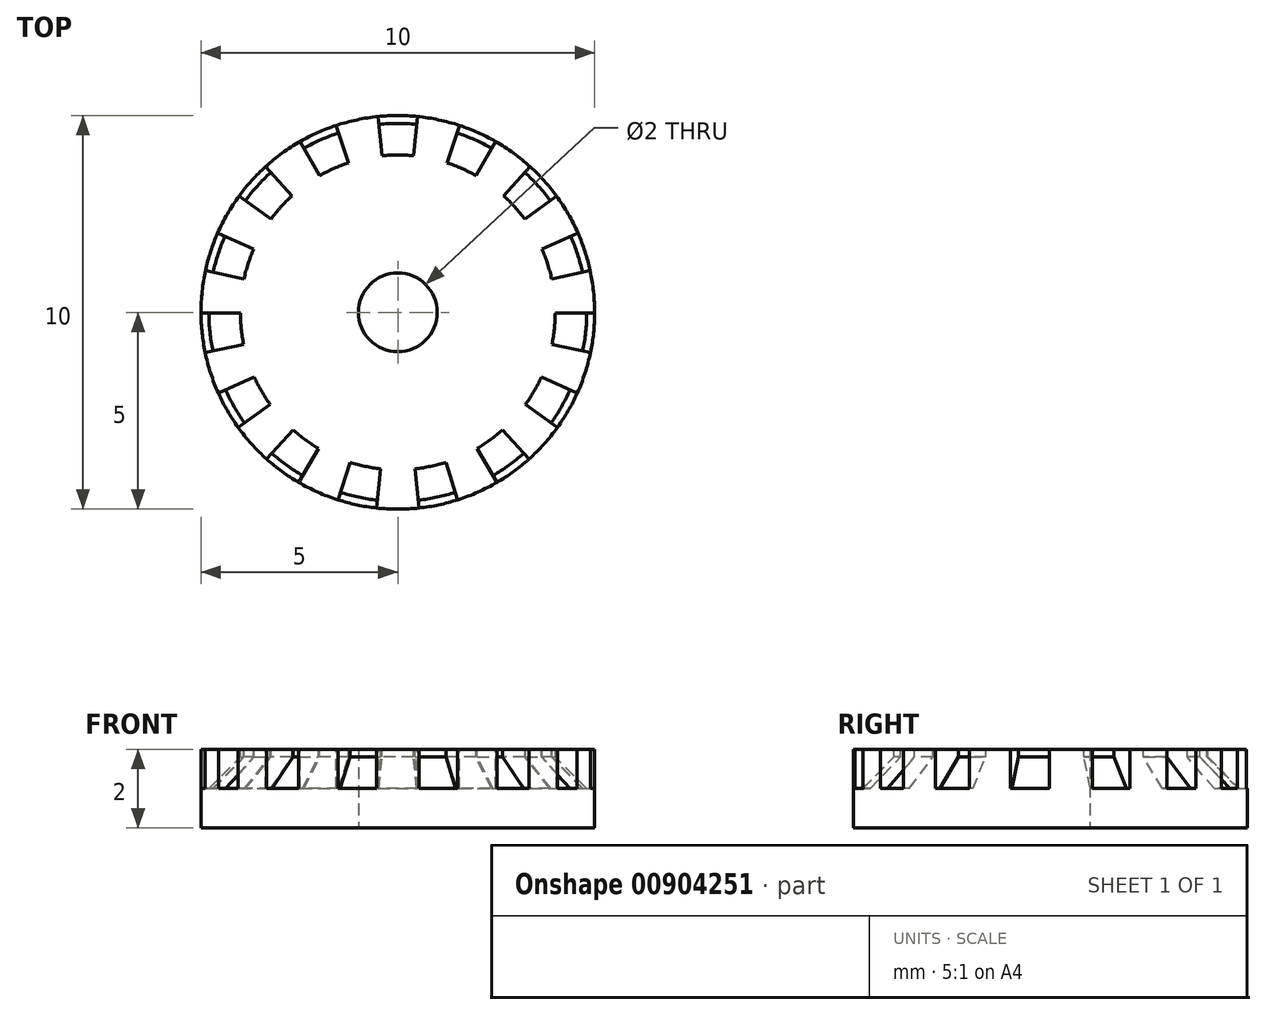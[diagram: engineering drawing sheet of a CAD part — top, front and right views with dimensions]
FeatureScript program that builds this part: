
annotation { "Feature Type Name" : "Feature", "Feature Type Description" : "" }
export const myFeature = defineFeature(function(context is Context, id is Id, definition is map)
    precondition{}
    {
        {
            var Q0;
            Q0=qCreatedBy(makeId("Front.planeOp"),FACE);
            var sketch = newSketch(context, id + "F0", { "sketchPlane" : qUnion([Q0])});
            skLineSegment(sketch, "E0.bottom", {"start": v(0, 0) * mm, "end": v(-5, 0) * mm});
            skLineSegment(sketch, "E0.top", {"start": v(0, 2) * mm, "end": v(-5, 2) * mm});
            skLineSegment(sketch, "E0.left", {"start": v(0, 0) * mm, "end": v(0, 2) * mm});
            skLineSegment(sketch, "E0.right", {"start": v(-5, 0) * mm, "end": v(-5, 2) * mm});
            skLineSegment(sketch, "E1", {"start": v(-1, 2) * mm, "end": v(-1, 0) * mm});
            skSolve(sketch);
        }
        {
            var Q0;
            {var subQ0=sQuery(id+"F0.wireOp",EDGE,"E0.right");Q0=makeQuery(id+"F0.imprint","IMPRINT",FACE,{"disambiguationData":[TD([[makeQuery(id+"F0.imprint","IMPRINT",EDGE,{"derivedFrom":subQ0}),-1.0]])]});}
            var Q1;
            Q1=sQuery(id+"F0.wireOp",EDGE,"E0.left");
            revolve(context, id + "F1", {"surfaceOperationType" : NewSurfaceOperationType.NEW, "entities" : qUnion([Q0]), "axis" : qUnion([Q1]), "revolveType" : RevolveType.FULL});
        }
        {
            var Q0;
            Q0=makeQuery(id+"F1.opRevolve","SWEPT_FACE",FACE,{"disambiguationData":[OSD([sQuery(id+"F0.wireOp",EDGE,"E0.top")])]});
            var sketch = newSketch(context, id + "F2", { "sketchPlane" : qUnion([Q0])});
            skLineSegment(sketch, "E2", {"start": v(0, 0) * mm, "end": v(0, 5) * mm});
            skLineSegment(sketch, "E3", {"start": v(-0.5, 4.97) * mm, "end": v(0.5, 4.97) * mm});
            skLineSegment(sketch, "E4", {"start": v(0, 0) * mm, "end": v(-0.5, 4.97) * mm});
            skLineSegment(sketch, "E5", {"start": v(0, 0) * mm, "end": v(0.5, 4.97) * mm});
            skCircle(sketch, "E6", {"center": v(0, 0) * mm, "radius": 4 * mm});
            skLineSegment(sketch, "E7", {"start": v(0, 0) * mm, "end": v(4, 0) * mm});
            skLineSegment(sketch, "E8", {"start": v(4, 0) * mm, "end": v(5, 0) * mm});
            skLineSegment(sketch, "E9.1.0", {"start": v(0, 0) * mm, "end": v(-2.48, 4.34) * mm});
            skLineSegment(sketch, "E9.1.1", {"start": v(0, 0) * mm, "end": v(-1.57, 4.75) * mm});
            skLineSegment(sketch, "E9.2.0", {"start": v(0, 0) * mm, "end": v(-4.03, 2.96) * mm});
            skLineSegment(sketch, "E9.2.1", {"start": v(0, 0) * mm, "end": v(-3.36, 3.7) * mm});
            skLineSegment(sketch, "E10.2.3.0", {"start": v(0, 0) * mm, "end": v(-4.89, 1.06) * mm});
            skLineSegment(sketch, "E10.3.3.0", {"start": v(0, 0) * mm, "end": v(-4.58, 2.01) * mm});
            skLineSegment(sketch, "E10.2.4.0", {"start": v(0, 0) * mm, "end": v(-4.9, -1.02) * mm});
            skLineSegment(sketch, "E10.3.4.0", {"start": v(0, 0) * mm, "end": v(-5, -0.02) * mm});
            skLineSegment(sketch, "E10.2.5.0", {"start": v(0, 0) * mm, "end": v(-4.06, -2.92) * mm});
            skLineSegment(sketch, "E10.3.5.0", {"start": v(0, 0) * mm, "end": v(-4.56, -2.05) * mm});
            skLineSegment(sketch, "E10.2.6.0", {"start": v(0, 0) * mm, "end": v(-2.52, -4.32) * mm});
            skLineSegment(sketch, "E10.3.6.0", {"start": v(0, 0) * mm, "end": v(-3.33, -3.73) * mm});
            skLineSegment(sketch, "E10.2.7.0", {"start": v(0, 0) * mm, "end": v(-0.55, -4.97) * mm});
            skLineSegment(sketch, "E10.3.7.0", {"start": v(0, 0) * mm, "end": v(-1.52, -4.76) * mm});
            skLineSegment(sketch, "E10.2.8.0", {"start": v(0, 0) * mm, "end": v(1.52, -4.76) * mm});
            skLineSegment(sketch, "E10.3.8.0", {"start": v(0, 0) * mm, "end": v(0.55, -4.97) * mm});
            skLineSegment(sketch, "E10.2.9.0", {"start": v(0, 0) * mm, "end": v(3.33, -3.73) * mm});
            skLineSegment(sketch, "E10.3.9.0", {"start": v(0, 0) * mm, "end": v(2.52, -4.32) * mm});
            skLineSegment(sketch, "E10.2.10.0", {"start": v(0, 0) * mm, "end": v(4.56, -2.05) * mm});
            skLineSegment(sketch, "E10.3.10.0", {"start": v(0, 0) * mm, "end": v(4.06, -2.92) * mm});
            skLineSegment(sketch, "E10.2.11.0", {"start": v(0, 0) * mm, "end": v(5, -0.02) * mm});
            skLineSegment(sketch, "E10.3.11.0", {"start": v(0, 0) * mm, "end": v(4.9, -1.02) * mm});
            skLineSegment(sketch, "E10.2.12.0", {"start": v(0, 0) * mm, "end": v(4.58, 2.01) * mm});
            skLineSegment(sketch, "E10.3.12.0", {"start": v(0, 0) * mm, "end": v(4.89, 1.06) * mm});
            skLineSegment(sketch, "E10.2.13.0", {"start": v(0, 0) * mm, "end": v(3.36, 3.7) * mm});
            skLineSegment(sketch, "E10.3.13.0", {"start": v(0, 0) * mm, "end": v(4.03, 2.96) * mm});
            skLineSegment(sketch, "E10.2.14.0", {"start": v(0, 0) * mm, "end": v(1.57, 4.75) * mm});
            skLineSegment(sketch, "E10.3.14.0", {"start": v(0, 0) * mm, "end": v(2.48, 4.34) * mm});
            skSolve(sketch);
        }
        {
            var Q0;
            {var subQ0=sQuery(id+"F2.wireOp",EDGE,"E6");var subQ1=sQuery(id+"F2.wireOp",EDGE,"E2");var subQ2=makeQuery(id+"F2.imprint","INTERSECT",VERTEX,{"derivedFrom":[subQ1,subQ0]});Q0=makeQuery(id+"F2.imprint","IMPRINT",FACE,{"disambiguationData":[TD([[makeQuery(id+"F2.imprint","IMPRINT",EDGE,{"disambiguationData":[TD([[subQ2,-1.0]])],"derivedFrom":subQ1}),1.0]])]});}
            var Q1;
            {var subQ0=sQuery(id+"F2.wireOp",EDGE,"E6");var subQ1=sQuery(id+"F2.wireOp",EDGE,"E2");var subQ2=makeQuery(id+"F2.imprint","INTERSECT",VERTEX,{"derivedFrom":[subQ1,subQ0]});Q1=makeQuery(id+"F2.imprint","IMPRINT",FACE,{"disambiguationData":[TD([[makeQuery(id+"F2.imprint","IMPRINT",EDGE,{"disambiguationData":[TD([[subQ2,-1.0]])],"derivedFrom":subQ1}),-1.0]])]});}
            var Q2;
            {var subQ0=sQuery(id+"F2.wireOp",EDGE,"E2");var subQ3=sQuery(id+"F2.wireOp",EDGE,"E3");var subQ4=makeQuery(id+"F2.imprint","INTERSECT",VERTEX,{"derivedFrom":[subQ0,subQ3]});Q2=makeQuery(id+"F2.imprint","IMPRINT",FACE,{"disambiguationData":[TD([[makeQuery(id+"F2.imprint","IMPRINT",EDGE,{"disambiguationData":[TD([[subQ4,-1.0]])],"derivedFrom":subQ0}),-1.0]])]});}
            var Q3;
            {var subQ0=sQuery(id+"F2.wireOp",EDGE,"E2");var subQ3=sQuery(id+"F2.wireOp",EDGE,"E3");var subQ4=makeQuery(id+"F2.imprint","INTERSECT",VERTEX,{"derivedFrom":[subQ0,subQ3]});Q3=makeQuery(id+"F2.imprint","IMPRINT",FACE,{"disambiguationData":[TD([[makeQuery(id+"F2.imprint","IMPRINT",EDGE,{"disambiguationData":[TD([[subQ4,-1.0]])],"derivedFrom":subQ0}),1.0]])]});}
            var Q4;
            {var subQ0=sQuery(id+"F2.wireOp",EDGE,"E10.3.14.0");var subQ1=sQuery(id+"F2.wireOp",EDGE,"E6");var subQ2=makeQuery(id+"F2.imprint","INTERSECT",VERTEX,{"derivedFrom":[subQ1,subQ0]});Q4=makeQuery(id+"F2.imprint","IMPRINT",FACE,{"disambiguationData":[TD([[makeQuery(id+"F2.imprint","IMPRINT",EDGE,{"disambiguationData":[TD([[subQ2,-1.0]])],"derivedFrom":subQ1}),-1.0]])]});}
            var Q5;
            {var subQ0=sQuery(id+"F2.wireOp",EDGE,"E10.3.13.0");var subQ1=sQuery(id+"F2.wireOp",EDGE,"E6");var subQ2=makeQuery(id+"F2.imprint","INTERSECT",VERTEX,{"derivedFrom":[subQ1,subQ0]});Q5=makeQuery(id+"F2.imprint","IMPRINT",FACE,{"disambiguationData":[TD([[makeQuery(id+"F2.imprint","IMPRINT",EDGE,{"disambiguationData":[TD([[subQ2,-1.0]])],"derivedFrom":subQ1}),-1.0]])]});}
            var Q6;
            {var subQ0=sQuery(id+"F2.wireOp",EDGE,"E10.3.12.0");var subQ1=sQuery(id+"F2.wireOp",EDGE,"E6");var subQ2=makeQuery(id+"F2.imprint","INTERSECT",VERTEX,{"derivedFrom":[subQ1,subQ0]});Q6=makeQuery(id+"F2.imprint","IMPRINT",FACE,{"disambiguationData":[TD([[makeQuery(id+"F2.imprint","IMPRINT",EDGE,{"disambiguationData":[TD([[subQ2,-1.0]])],"derivedFrom":subQ1}),-1.0]])]});}
            var Q7;
            {var subQ0=sQuery(id+"F2.wireOp",EDGE,"E10.3.11.0");var subQ1=sQuery(id+"F2.wireOp",EDGE,"E6");var subQ2=makeQuery(id+"F2.imprint","INTERSECT",VERTEX,{"derivedFrom":[subQ1,subQ0]});Q7=makeQuery(id+"F2.imprint","IMPRINT",FACE,{"disambiguationData":[TD([[makeQuery(id+"F2.imprint","IMPRINT",EDGE,{"disambiguationData":[TD([[subQ2,-1.0]])],"derivedFrom":subQ1}),-1.0]])]});}
            var Q8;
            {var subQ0=sQuery(id+"F2.wireOp",EDGE,"E10.3.10.0");var subQ1=sQuery(id+"F2.wireOp",EDGE,"E6");var subQ2=makeQuery(id+"F2.imprint","INTERSECT",VERTEX,{"derivedFrom":[subQ1,subQ0]});Q8=makeQuery(id+"F2.imprint","IMPRINT",FACE,{"disambiguationData":[TD([[makeQuery(id+"F2.imprint","IMPRINT",EDGE,{"disambiguationData":[TD([[subQ2,-1.0]])],"derivedFrom":subQ1}),-1.0]])]});}
            var Q9;
            {var subQ0=sQuery(id+"F2.wireOp",EDGE,"E10.3.9.0");var subQ1=sQuery(id+"F2.wireOp",EDGE,"E6");var subQ2=makeQuery(id+"F2.imprint","INTERSECT",VERTEX,{"derivedFrom":[subQ1,subQ0]});Q9=makeQuery(id+"F2.imprint","IMPRINT",FACE,{"disambiguationData":[TD([[makeQuery(id+"F2.imprint","IMPRINT",EDGE,{"disambiguationData":[TD([[subQ2,-1.0]])],"derivedFrom":subQ1}),-1.0]])]});}
            var Q10;
            {var subQ0=sQuery(id+"F2.wireOp",EDGE,"E10.3.8.0");var subQ1=sQuery(id+"F2.wireOp",EDGE,"E6");var subQ2=makeQuery(id+"F2.imprint","INTERSECT",VERTEX,{"derivedFrom":[subQ1,subQ0]});Q10=makeQuery(id+"F2.imprint","IMPRINT",FACE,{"disambiguationData":[TD([[makeQuery(id+"F2.imprint","IMPRINT",EDGE,{"disambiguationData":[TD([[subQ2,-1.0]])],"derivedFrom":subQ1}),-1.0]])]});}
            var Q11;
            {var subQ0=sQuery(id+"F2.wireOp",EDGE,"E10.3.7.0");var subQ1=sQuery(id+"F2.wireOp",EDGE,"E6");var subQ2=makeQuery(id+"F2.imprint","INTERSECT",VERTEX,{"derivedFrom":[subQ1,subQ0]});Q11=makeQuery(id+"F2.imprint","IMPRINT",FACE,{"disambiguationData":[TD([[makeQuery(id+"F2.imprint","IMPRINT",EDGE,{"disambiguationData":[TD([[subQ2,-1.0]])],"derivedFrom":subQ1}),-1.0]])]});}
            var Q12;
            {var subQ0=sQuery(id+"F2.wireOp",EDGE,"E10.3.6.0");var subQ1=sQuery(id+"F2.wireOp",EDGE,"E6");var subQ2=makeQuery(id+"F2.imprint","INTERSECT",VERTEX,{"derivedFrom":[subQ1,subQ0]});Q12=makeQuery(id+"F2.imprint","IMPRINT",FACE,{"disambiguationData":[TD([[makeQuery(id+"F2.imprint","IMPRINT",EDGE,{"disambiguationData":[TD([[subQ2,-1.0]])],"derivedFrom":subQ1}),-1.0]])]});}
            var Q13;
            {var subQ0=sQuery(id+"F2.wireOp",EDGE,"E10.3.5.0");var subQ1=sQuery(id+"F2.wireOp",EDGE,"E6");var subQ2=makeQuery(id+"F2.imprint","INTERSECT",VERTEX,{"derivedFrom":[subQ1,subQ0]});Q13=makeQuery(id+"F2.imprint","IMPRINT",FACE,{"disambiguationData":[TD([[makeQuery(id+"F2.imprint","IMPRINT",EDGE,{"disambiguationData":[TD([[subQ2,-1.0]])],"derivedFrom":subQ1}),-1.0]])]});}
            var Q14;
            {var subQ0=sQuery(id+"F2.wireOp",EDGE,"E10.3.4.0");var subQ1=sQuery(id+"F2.wireOp",EDGE,"E6");var subQ2=makeQuery(id+"F2.imprint","INTERSECT",VERTEX,{"derivedFrom":[subQ1,subQ0]});Q14=makeQuery(id+"F2.imprint","IMPRINT",FACE,{"disambiguationData":[TD([[makeQuery(id+"F2.imprint","IMPRINT",EDGE,{"disambiguationData":[TD([[subQ2,-1.0]])],"derivedFrom":subQ1}),-1.0]])]});}
            var Q15;
            {var subQ0=sQuery(id+"F2.wireOp",EDGE,"E10.3.3.0");var subQ1=sQuery(id+"F2.wireOp",EDGE,"E6");var subQ2=makeQuery(id+"F2.imprint","INTERSECT",VERTEX,{"derivedFrom":[subQ1,subQ0]});Q15=makeQuery(id+"F2.imprint","IMPRINT",FACE,{"disambiguationData":[TD([[makeQuery(id+"F2.imprint","IMPRINT",EDGE,{"disambiguationData":[TD([[subQ2,-1.0]])],"derivedFrom":subQ1}),-1.0]])]});}
            var Q16;
            {var subQ0=sQuery(id+"F2.wireOp",EDGE,"E9.2.1");var subQ1=sQuery(id+"F2.wireOp",EDGE,"E6");var subQ2=makeQuery(id+"F2.imprint","INTERSECT",VERTEX,{"derivedFrom":[subQ1,subQ0]});Q16=makeQuery(id+"F2.imprint","IMPRINT",FACE,{"disambiguationData":[TD([[makeQuery(id+"F2.imprint","IMPRINT",EDGE,{"disambiguationData":[TD([[subQ2,-1.0]])],"derivedFrom":subQ1}),-1.0]])]});}
            var Q17;
            {var subQ0=sQuery(id+"F2.wireOp",EDGE,"E9.1.1");var subQ1=sQuery(id+"F2.wireOp",EDGE,"E6");var subQ2=makeQuery(id+"F2.imprint","INTERSECT",VERTEX,{"derivedFrom":[subQ1,subQ0]});Q17=makeQuery(id+"F2.imprint","IMPRINT",FACE,{"disambiguationData":[TD([[makeQuery(id+"F2.imprint","IMPRINT",EDGE,{"disambiguationData":[TD([[subQ2,-1.0]])],"derivedFrom":subQ1}),-1.0]])]});}
            extrude(context, id + "F3", {"entities" : qUnion([Q0, Q1, Q2, Q3, Q4, Q5, Q6, Q7, Q8, Q9, Q10, Q11, Q12, Q13, Q14, Q15, Q16, Q17]), "operationType" : NewBodyOperationType.REMOVE, "oppositeDirection" : true, "depth" : 1 * mm, "offsetDistance" : 25 * mm});
        }
        {
            var Q0;
            {var subQ0=sQuery(id+"F2.wireOp",EDGE,"E6");Q0=makeQuery(id+"F3.boolean.opBoolean","COPY",EDGE,{"derivedFrom":makeQuery(id+"F3.opExtrude","CAP_EDGE",EDGE,{"disambiguationData":[OSD([subQ0]),TDD([makeQuery(id+"F2.imprint","IMPRINT",EDGE,{"disambiguationData":[TD([[makeQuery(id+"F2.imprint","INTERSECT",VERTEX,{"derivedFrom":[subQ0,sQuery(id+"F2.wireOp",EDGE,"E10.3.4.0")]}),-1.0]])],"derivedFrom":subQ0})])],"isStart":false})});}
            var Q1;
            {var subQ0=sQuery(id+"F2.wireOp",EDGE,"E6");Q1=makeQuery(id+"F3.boolean.opBoolean","COPY",EDGE,{"derivedFrom":makeQuery(id+"F3.opExtrude","CAP_EDGE",EDGE,{"disambiguationData":[OSD([subQ0]),TDD([makeQuery(id+"F2.imprint","IMPRINT",EDGE,{"disambiguationData":[TD([[makeQuery(id+"F2.imprint","INTERSECT",VERTEX,{"derivedFrom":[subQ0,sQuery(id+"F2.wireOp",EDGE,"E10.3.5.0")]}),-1.0]])],"derivedFrom":subQ0})])],"isStart":false})});}
            var Q2;
            {var subQ0=sQuery(id+"F2.wireOp",EDGE,"E6");Q2=makeQuery(id+"F3.boolean.opBoolean","COPY",EDGE,{"derivedFrom":makeQuery(id+"F3.opExtrude","CAP_EDGE",EDGE,{"disambiguationData":[OSD([subQ0]),TDD([makeQuery(id+"F2.imprint","IMPRINT",EDGE,{"disambiguationData":[TD([[makeQuery(id+"F2.imprint","INTERSECT",VERTEX,{"derivedFrom":[subQ0,sQuery(id+"F2.wireOp",EDGE,"E10.3.6.0")]}),-1.0]])],"derivedFrom":subQ0})])],"isStart":false})});}
            var Q3;
            {var subQ0=sQuery(id+"F2.wireOp",EDGE,"E6");Q3=makeQuery(id+"F3.boolean.opBoolean","COPY",EDGE,{"derivedFrom":makeQuery(id+"F3.opExtrude","CAP_EDGE",EDGE,{"disambiguationData":[OSD([subQ0]),TDD([makeQuery(id+"F2.imprint","IMPRINT",EDGE,{"disambiguationData":[TD([[makeQuery(id+"F2.imprint","INTERSECT",VERTEX,{"derivedFrom":[subQ0,sQuery(id+"F2.wireOp",EDGE,"E10.3.7.0")]}),-1.0]])],"derivedFrom":subQ0})])],"isStart":false})});}
            var Q4;
            {var subQ0=sQuery(id+"F2.wireOp",EDGE,"E6");Q4=makeQuery(id+"F3.boolean.opBoolean","COPY",EDGE,{"derivedFrom":makeQuery(id+"F3.opExtrude","CAP_EDGE",EDGE,{"disambiguationData":[OSD([subQ0]),TDD([makeQuery(id+"F2.imprint","IMPRINT",EDGE,{"disambiguationData":[TD([[makeQuery(id+"F2.imprint","INTERSECT",VERTEX,{"derivedFrom":[subQ0,sQuery(id+"F2.wireOp",EDGE,"E10.3.8.0")]}),-1.0]])],"derivedFrom":subQ0})])],"isStart":false})});}
            var Q5;
            {var subQ0=sQuery(id+"F2.wireOp",EDGE,"E6");Q5=makeQuery(id+"F3.boolean.opBoolean","COPY",EDGE,{"derivedFrom":makeQuery(id+"F3.opExtrude","CAP_EDGE",EDGE,{"disambiguationData":[OSD([subQ0]),TDD([makeQuery(id+"F2.imprint","IMPRINT",EDGE,{"disambiguationData":[TD([[makeQuery(id+"F2.imprint","INTERSECT",VERTEX,{"derivedFrom":[subQ0,sQuery(id+"F2.wireOp",EDGE,"E10.3.9.0")]}),-1.0]])],"derivedFrom":subQ0})])],"isStart":false})});}
            var Q6;
            {var subQ0=sQuery(id+"F2.wireOp",EDGE,"E6");Q6=makeQuery(id+"F3.boolean.opBoolean","COPY",EDGE,{"derivedFrom":makeQuery(id+"F3.opExtrude","CAP_EDGE",EDGE,{"disambiguationData":[OSD([subQ0]),TDD([makeQuery(id+"F2.imprint","IMPRINT",EDGE,{"disambiguationData":[TD([[makeQuery(id+"F2.imprint","INTERSECT",VERTEX,{"derivedFrom":[subQ0,sQuery(id+"F2.wireOp",EDGE,"E10.3.10.0")]}),-1.0]])],"derivedFrom":subQ0})])],"isStart":false})});}
            var Q7;
            {var subQ0=sQuery(id+"F2.wireOp",EDGE,"E6");Q7=makeQuery(id+"F3.boolean.opBoolean","COPY",EDGE,{"derivedFrom":makeQuery(id+"F3.opExtrude","CAP_EDGE",EDGE,{"disambiguationData":[OSD([subQ0]),TDD([makeQuery(id+"F2.imprint","IMPRINT",EDGE,{"disambiguationData":[TD([[makeQuery(id+"F2.imprint","INTERSECT",VERTEX,{"derivedFrom":[subQ0,sQuery(id+"F2.wireOp",EDGE,"E10.3.11.0")]}),-1.0]])],"derivedFrom":subQ0})])],"isStart":false})});}
            var Q8;
            {var subQ0=sQuery(id+"F2.wireOp",EDGE,"E6");Q8=makeQuery(id+"F3.boolean.opBoolean","COPY",EDGE,{"derivedFrom":makeQuery(id+"F3.opExtrude","CAP_EDGE",EDGE,{"disambiguationData":[OSD([subQ0]),TDD([makeQuery(id+"F2.imprint","IMPRINT",EDGE,{"disambiguationData":[TD([[makeQuery(id+"F2.imprint","INTERSECT",VERTEX,{"derivedFrom":[subQ0,sQuery(id+"F2.wireOp",EDGE,"E10.3.12.0")]}),-1.0]])],"derivedFrom":subQ0})])],"isStart":false})});}
            var Q9;
            {var subQ0=sQuery(id+"F2.wireOp",EDGE,"E6");Q9=makeQuery(id+"F3.boolean.opBoolean","COPY",EDGE,{"derivedFrom":makeQuery(id+"F3.opExtrude","CAP_EDGE",EDGE,{"disambiguationData":[OSD([subQ0]),TDD([makeQuery(id+"F2.imprint","IMPRINT",EDGE,{"disambiguationData":[TD([[makeQuery(id+"F2.imprint","INTERSECT",VERTEX,{"derivedFrom":[subQ0,sQuery(id+"F2.wireOp",EDGE,"E10.3.13.0")]}),-1.0]])],"derivedFrom":subQ0})])],"isStart":false})});}
            var Q10;
            {var subQ0=sQuery(id+"F2.wireOp",EDGE,"E6");Q10=makeQuery(id+"F3.boolean.opBoolean","COPY",EDGE,{"derivedFrom":makeQuery(id+"F3.opExtrude","CAP_EDGE",EDGE,{"disambiguationData":[OSD([subQ0]),TDD([makeQuery(id+"F2.imprint","IMPRINT",EDGE,{"disambiguationData":[TD([[makeQuery(id+"F2.imprint","INTERSECT",VERTEX,{"derivedFrom":[subQ0,sQuery(id+"F2.wireOp",EDGE,"E10.3.14.0")]}),-1.0]])],"derivedFrom":subQ0})])],"isStart":false})});}
            var Q11;
            {var subQ0=sQuery(id+"F2.wireOp",EDGE,"E6");var subQ1=makeQuery(id+"F2.imprint","INTERSECT",VERTEX,{"derivedFrom":[sQuery(id+"F2.wireOp",EDGE,"E2"),subQ0]});Q11=makeQuery(id+"F3.boolean.opBoolean","COPY",EDGE,{"derivedFrom":makeQuery(id+"F3.opExtrude","CAP_EDGE",EDGE,{"disambiguationData":[OSD([subQ0]),TDD([makeQuery(id+"F2.imprint","IMPRINT",EDGE,{"disambiguationData":[TD([[subQ1,1.0]])],"derivedFrom":subQ0}),makeQuery(id+"F2.imprint","IMPRINT",EDGE,{"disambiguationData":[TD([[subQ1,-1.0]])],"derivedFrom":subQ0})])],"isStart":false})});}
            var Q12;
            {var subQ0=sQuery(id+"F2.wireOp",EDGE,"E6");Q12=makeQuery(id+"F3.boolean.opBoolean","COPY",EDGE,{"derivedFrom":makeQuery(id+"F3.opExtrude","CAP_EDGE",EDGE,{"disambiguationData":[OSD([subQ0]),TDD([makeQuery(id+"F2.imprint","IMPRINT",EDGE,{"disambiguationData":[TD([[makeQuery(id+"F2.imprint","INTERSECT",VERTEX,{"derivedFrom":[subQ0,sQuery(id+"F2.wireOp",EDGE,"E9.1.1")]}),-1.0]])],"derivedFrom":subQ0})])],"isStart":false})});}
            var Q13;
            {var subQ0=sQuery(id+"F2.wireOp",EDGE,"E6");Q13=makeQuery(id+"F3.boolean.opBoolean","COPY",EDGE,{"derivedFrom":makeQuery(id+"F3.opExtrude","CAP_EDGE",EDGE,{"disambiguationData":[OSD([subQ0]),TDD([makeQuery(id+"F2.imprint","IMPRINT",EDGE,{"disambiguationData":[TD([[makeQuery(id+"F2.imprint","INTERSECT",VERTEX,{"derivedFrom":[subQ0,sQuery(id+"F2.wireOp",EDGE,"E9.2.1")]}),-1.0]])],"derivedFrom":subQ0})])],"isStart":false})});}
            var Q14;
            {var subQ0=sQuery(id+"F2.wireOp",EDGE,"E6");Q14=makeQuery(id+"F3.boolean.opBoolean","COPY",EDGE,{"derivedFrom":makeQuery(id+"F3.opExtrude","CAP_EDGE",EDGE,{"disambiguationData":[OSD([subQ0]),TDD([makeQuery(id+"F2.imprint","IMPRINT",EDGE,{"disambiguationData":[TD([[makeQuery(id+"F2.imprint","INTERSECT",VERTEX,{"derivedFrom":[subQ0,sQuery(id+"F2.wireOp",EDGE,"E10.3.3.0")]}),-1.0]])],"derivedFrom":subQ0})])],"isStart":false})});}
            chamfer(context, id + "F4", {"entities" : qUnion([Q0, Q1, Q2, Q3, Q4, Q5, Q6, Q7, Q8, Q9, Q10, Q11, Q12, Q13, Q14]), "width" : 0.8 * mm, "tangentPropagation" : true});
        }
    });
